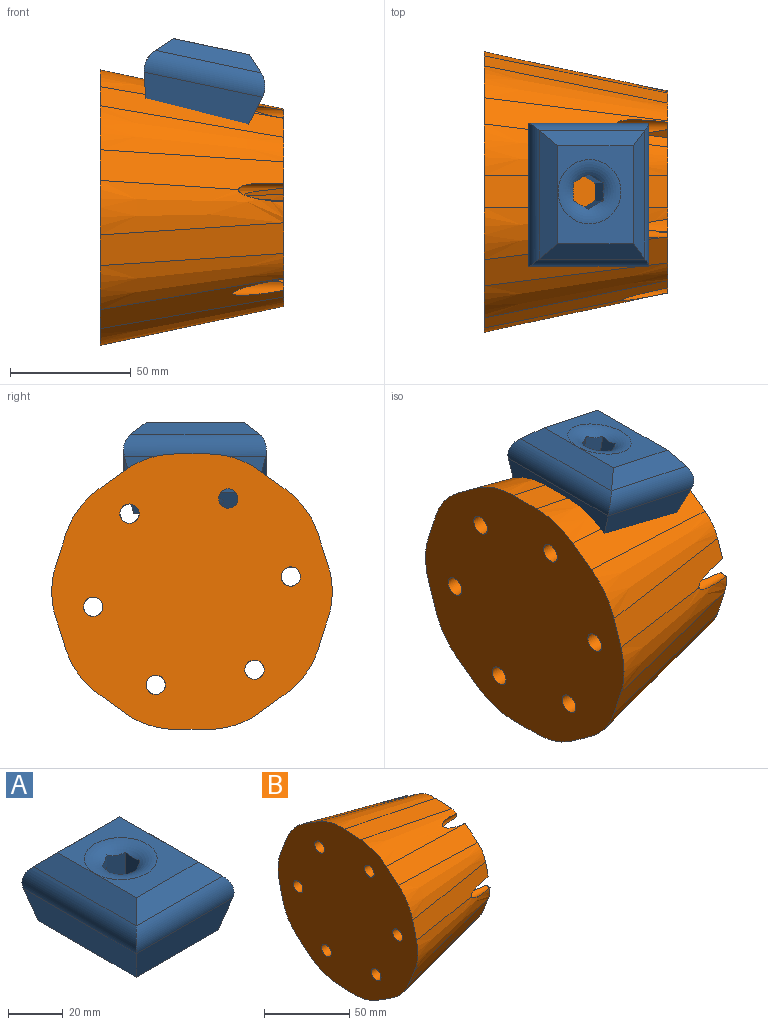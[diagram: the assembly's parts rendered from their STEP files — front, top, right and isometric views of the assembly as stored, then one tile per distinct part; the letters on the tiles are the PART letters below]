
ASSEMBLY  parts=2 mates=1
PART A: 23 faces, bbox 51.4x59.9x31.2 mm
  f0: torus R=13.33mm, axis (0,0,-1), area 570.6mm2, adj f5,f22
  f1: torus R=13.33mm, axis (0,0,-1), area 451.1mm2, adj f3,f16,f17,f18,f19,f20,f21
  f2: plane 58.54x14.45mm, normal (0.97,0,-0.26), area 817.9mm2, adj f5,f6,f7,f12
  f3: plane 40.64x32.12mm, normal (0,0,1), area 746.6mm2, adj f1,f8,f9,f10,f11
  f4: plane 58.54x14.45mm, normal (-0.97,0,-0.26), area 817.9mm2, adj f5,f6,f7,f15
  f5: plane 50.8x42.28mm, normal (0,0,-1), area 1589mm2, adj f0,f2,f4,f6,f7
  f6: plane 50.02x14.45mm, normal (0,-0.97,-0.26), area 690.4mm2, adj f2,f4,f5,f13
  f7: plane 50.02x14.45mm, normal (0,0.97,-0.26), area 690.4mm2, adj f2,f4,f5,f14
  f8: plane 53.28x6.32mm, normal (-0.71,0,0.71), area 419.9mm2, adj f3,f9,f10,f15
  f9: plane 44.76x6.32mm, normal (0,-0.71,0.71), area 343.7mm2, adj f3,f8,f11,f13
  f10: plane 44.76x6.32mm, normal (0,0.71,0.71), area 343.7mm2, adj f3,f8,f11,f14
  f11: plane 53.28x6.32mm, normal (0.71,0,0.71), area 419.9mm2, adj f3,f9,f10,f12
  f12: cylinder r=10.16mm len=59.24mm, axis (0,1,0), area 613.5mm2, adj f2,f11,f13,f14
  f13: cylinder r=10.16mm len=50.72mm, axis (1,0,0), area 522.8mm2, adj f6,f9,f12,f15
  f14: cylinder r=10.16mm len=50.72mm, axis (-1,0,0), area 522.8mm2, adj f7,f10,f12,f15
  f15: cylinder r=10.16mm len=59.24mm, axis (0,1,0), area 613.5mm2, adj f4,f8,f13,f14
  f16: plane 24.05x7.93mm, normal (1,0,0), area 166.7mm2, adj f1,f17,f21,f22
  f17: plane 23.4x6.31mm, normal (0.5,0.87,0), area 166.7mm2, adj f1,f16,f18,f22
  f18: plane 23.4x6.31mm, normal (-0.5,0.87,0), area 166.7mm2, adj f1,f17,f19,f22
  f19: plane 23.41x7.29mm, normal (-1,0,0), area 166.7mm2, adj f1,f18,f20,f22
  f20: plane 23.4x6.31mm, normal (-0.5,-0.87,0), area 166.7mm2, adj f1,f19,f21,f22
  f21: plane 23.4x6.31mm, normal (0.5,-0.87,0), area 166.7mm2, adj f1,f16,f20,f22
  f22: plane 14.58x12.62mm, normal (0,0,1), area 75mm2, adj f0,f16,f17,f18,f19,f20,f21
PART B: 54 faces, bbox 76.2x116.2x115.1 mm
  f0: plane 31.63x18.25mm, normal (1,0,0), area 98.7mm2, adj f13,f14,f23,f24,f34,f35,f44,f45
  f1: plane 30.15x21.2mm, normal (1,0,0), area 98.7mm2, adj f6,f7,f17,f27,f28,f38,f47,f48
  f2: plane 34.19x8.84mm, normal (1,0,0), area 98.9mm2, adj f14,f15,f25,f26,f35,f36,f46,f47
  f3: plane 30.15x21.2mm, normal (1,0,0), area 98.7mm2, adj f11,f12,f22,f32,f33,f42,f43,f49
  f4: plane 34.19x8.84mm, normal (1,0,0), area 98.9mm2, adj f9,f10,f20,f21,f30,f31,f41,f42
  f5: plane 31.63x18.25mm, normal (1,0,0), area 98.7mm2, adj f8,f9,f18,f19,f29,f30,f39,f40
  f6: plane 76.21x21.01mm, normal (0.21,-0.63,0.75), area 1041.9mm2, adj f1,f16,f17,f26,f48
  f7: plane 76.2x18.93mm, normal (0.21,-0.95,0.23), area 981.4mm2, adj f1,f16,f17,f18,f51
  f8: plane 76.2x20.05mm, normal (0.21,-0.91,-0.37), area 1042mm2, adj f5,f16,f18,f19
  f9: plane 76.2x20.82mm, normal (0.21,-0.52,-0.83), area 901.6mm2, adj f4,f5,f16,f19,f20,f53
  f10: plane 76.2x17.13mm, normal (0.21,0.07,-0.98), area 1042mm2, adj f4,f16,f20,f21
  f11: plane 76.21x21.01mm, normal (0.21,0.63,-0.75), area 1041.9mm2, adj f3,f16,f21,f22,f50
  f12: plane 76.23x18.96mm, normal (0.21,0.95,-0.23), area 981.4mm2, adj f3,f16,f22,f23,f49
  f13: plane 76.2x20.05mm, normal (0.21,0.91,0.37), area 1042mm2, adj f0,f16,f23,f24
  f14: plane 76.2x20.82mm, normal (0.21,0.52,0.83), area 901.6mm2, adj f0,f2,f16,f24,f25,f52
  f15: plane 76.2x17.13mm, normal (0.21,-0.07,0.98), area 1042mm2, adj f2,f16,f25,f26
  f16: plane 116.21x115.06mm, normal (-1,0,0), area 10147.6mm2, adj f6,f7,f8,f9,f10,f11,f12,f13
  f17: cone r=20.32mm half-angle=12deg, axis (-1,0,0), area 1391mm2, adj f1,f6,f7,f16
  f18: cone r=20.32mm half-angle=12deg, axis (-1,0,0), area 1327.8mm2, adj f5,f7,f8,f16,f51
  f19: cone r=20.32mm half-angle=12deg, axis (-1,0,0), area 1391mm2, adj f5,f8,f9,f16
  f20: cone r=20.32mm half-angle=12deg, axis (-1,0,0), area 1391mm2, adj f4,f9,f10,f16
  f21: cone r=20.32mm half-angle=12deg, axis (-1,0,0), area 1281.7mm2, adj f4,f10,f11,f16,f50
  f22: cone r=20.32mm half-angle=12deg, axis (-1,0,0), area 1391mm2, adj f3,f11,f12,f16
  f23: cone r=20.32mm half-angle=12deg, axis (-1,0,0), area 1327.8mm2, adj f0,f12,f13,f16,f49
  f24: cone r=20.32mm half-angle=12deg, axis (-1,0,0), area 1391mm2, adj f0,f13,f14,f16
  f25: cone r=20.32mm half-angle=12deg, axis (-1,0,0), area 1391mm2, adj f2,f14,f15,f16
  f26: cone r=20.32mm half-angle=12deg, axis (-1,0,0), area 1281.7mm2, adj f2,f6,f15,f16,f48
  f27: plane 68.58x13.32mm, normal (0.07,0.64,-0.76), area 919.6mm2, adj f1,f37,f38,f47
  f28: plane 68.58x14.13mm, normal (0.07,0.97,-0.24), area 886.3mm2, adj f1,f37,f38,f39,f51
  f29: plane 68.58x14.2mm, normal (0.07,0.92,0.38), area 919.6mm2, adj f5,f37,f39,f40
  f30: plane 68.58x13.89mm, normal (0.07,0.53,0.85), area 889.6mm2, adj f4,f5,f37,f40,f41,f53
  f31: plane 68.58x13.69mm, normal (0.07,-0.07,0.99), area 919.6mm2, adj f4,f37,f41,f42
  f32: plane 68.58x13.32mm, normal (0.07,-0.64,0.76), area 919.6mm2, adj f3,f37,f42,f43
  f33: plane 68.58x14.13mm, normal (0.07,-0.97,0.24), area 886.3mm2, adj f3,f37,f43,f44,f49
  f34: plane 68.58x14.2mm, normal (0.07,-0.92,-0.38), area 919.6mm2, adj f0,f37,f44,f45
  f35: plane 68.6x13.91mm, normal (0.07,-0.53,-0.85), area 889.6mm2, adj f0,f2,f37,f45,f46,f52
  f36: plane 68.58x13.69mm, normal (0.07,0.07,-0.99), area 919.6mm2, adj f2,f37,f46,f47
  f37: plane 68.57x67.43mm, normal (1,0,0), area 3582.1mm2, adj f27,f28,f29,f30,f31,f32,f33,f34
  f38: cone r=12.7mm half-angle=4deg, axis (1,0,0), area 652.2mm2, adj f1,f27,f28,f37
  f39: cone r=12.7mm half-angle=4deg, axis (1,0,0), area 621.7mm2, adj f5,f28,f29,f37,f51
  f40: cone r=12.7mm half-angle=4deg, axis (1,0,0), area 652.2mm2, adj f5,f29,f30,f37
  f41: cone r=12.7mm half-angle=4deg, axis (1,0,0), area 652.2mm2, adj f4,f30,f31,f37
  f42: cone r=12.7mm half-angle=4deg, axis (1,0,0), area 553.3mm2, adj f3,f4,f31,f32,f37,f50
  f43: cone r=12.7mm half-angle=4deg, axis (1,0,0), area 652.2mm2, adj f3,f32,f33,f37
  f44: cone r=12.7mm half-angle=4deg, axis (1,0,0), area 621.7mm2, adj f0,f33,f34,f37,f49
  f45: cone r=12.7mm half-angle=4deg, axis (1,0,0), area 652.2mm2, adj f0,f34,f35,f37
  f46: cone r=12.7mm half-angle=4deg, axis (1,0,0), area 652.2mm2, adj f2,f35,f36,f37
  f47: cone r=12.7mm half-angle=4deg, axis (1,0,0), area 554.4mm2, adj f1,f2,f27,f36,f37,f48
  f48: cylinder r=4.01mm len=76.2mm, axis (1,0,0), area 1680.3mm2, adj f1,f2,f6,f16,f26,f47
  f49: cylinder r=4.01mm len=76.2mm, axis (1,0,0), area 1694.7mm2, adj f0,f3,f12,f16,f23,f33,f44
  f50: cylinder r=4.01mm len=76.2mm, axis (1,0,0), area 1684.4mm2, adj f3,f4,f11,f16,f21,f42
  f51: cylinder r=4.01mm len=76.2mm, axis (1,0,0), area 1694.7mm2, adj f1,f5,f7,f16,f18,f28,f39
  f52: cylinder r=4.01mm len=76.2mm, axis (1,0,0), area 1706mm2, adj f0,f2,f14,f16,f35
  f53: cylinder r=4.01mm len=76.2mm, axis (1,0,0), area 1706mm2, adj f4,f5,f9,f16,f30
PLACE A rot(axis=(0,1,0),12deg) t=(-6.43,-7.55,-1.61)mm
PLACE B rot(axis=(-1,0,0),4.2deg) t=(-73.24,-31.69,-63.97)mm
MATE planar B.f15 <-> A.f0  axis (0.21,0,0.98) through (-35.14,-31.69,-14.97)mm
